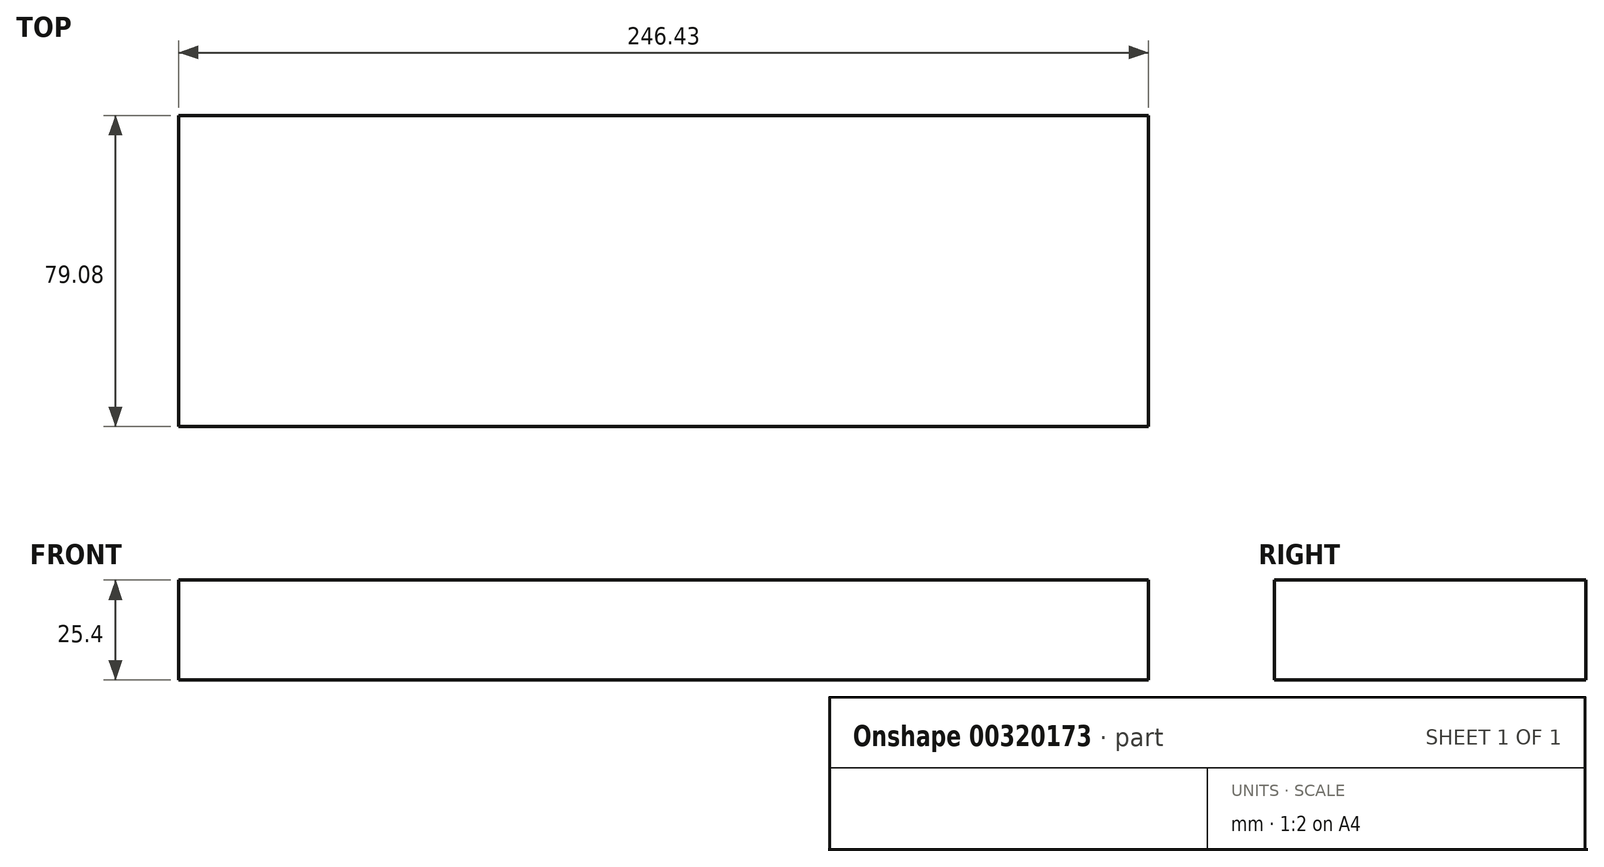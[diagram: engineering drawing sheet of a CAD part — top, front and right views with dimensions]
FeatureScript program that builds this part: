
annotation { "Feature Type Name" : "Feature", "Feature Type Description" : "" }
export const myFeature = defineFeature(function(context is Context, id is Id, definition is map)
    precondition{}
    {
        {
            var Q0;
            Q0=qCreatedBy(makeId("Top.planeOp"),FACE);
            var sketch = newSketch(context, id + "F0", { "sketchPlane" : qUnion([Q0])});
            skLineSegment(sketch, "E0.bottom", {"start": v(-118.77, 35.41) * mm, "end": v(127.66, 35.41) * mm});
            skLineSegment(sketch, "E0.top", {"start": v(-118.77, -43.67) * mm, "end": v(127.66, -43.67) * mm});
            skLineSegment(sketch, "E0.left", {"start": v(-118.77, 35.41) * mm, "end": v(-118.77, -43.67) * mm});
            skLineSegment(sketch, "E0.right", {"start": v(127.66, 35.41) * mm, "end": v(127.66, -43.67) * mm});
            skSolve(sketch);
        }
        {
            var Q0;
            Q0=makeQuery(id+"F0.imprint","IMPRINT",FACE,{"disambiguationData":[TD([[makeQuery(id+"F0.imprint","IMPRINT",EDGE,{"derivedFrom":sQuery(id+"F0.wireOp",EDGE,"E0.bottom")}),-1.0]])]});
            extrude(context, id + "F1", {"entities" : qUnion([Q0]), "depth" : 25.4 * mm});
        }
    });
